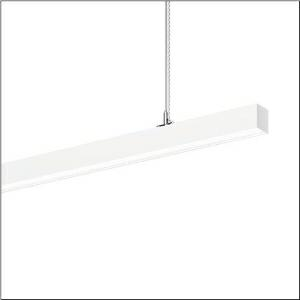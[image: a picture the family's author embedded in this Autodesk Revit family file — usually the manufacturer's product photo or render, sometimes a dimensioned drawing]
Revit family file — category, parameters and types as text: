
# Revit family: silica_r__21_51mx33dc3dwb_1062
name_source: partatom
category: Lighting Fixtures
units: mm (PartAtom-declared; Revit-internal decimal feet)

## family parameters
Cut with Voids When Loaded = No
Host = Face
Light Source = No
Part Type = Normal
Room Calculation Point = No
Round Connector Dimension = Use Diameter
Shared = No

## types (1)
- --- (1 x LED, 14780 lm, 99.5 W, 3000K)
    Apparent Load = 100 VA
    CIE Flux Codes = 78 96 99 55 100
    Color Rendering = 80
    Color Temperature = 3000K
    Default Elevation = 1800 mm
    Description = Silica® 21, office luminaire, primary optical cover: prismatic diffuser, of PMMA, CAT 2 (L<= 3000cd/m²), light emission: direct/indirect distribution, primary light characteristic: symmetric, installation type: suspended mounting, LED, rated luminous flux: 14.780lm, luminous efficacy: 149lm/W, light colour: 830, colour temperature: 3000K, control gear: DALI 2, with terminal, 3+2-pole, max. 2.5mm², mains connection: 220..240V, AC, 50/60Hz, rated input power: 99.5W, luminaire housing, of aluminium, traffic white (RAL 9016), length: 3.004mm, width: 53mm, height: 53mm, protection rating (complete): IP20, insulation class (complete): insulation class I (protective earthing), certification: CE, permissible operating ambient temperature: 0..+35°C, standard: EN 50419, packaging unit: 1 piece
    Height = 53 mm
    Lamp = 1 x LED
    Lamp Light Flux = 14780 lm
    Lamp Power = 99.5 W
    Lamp count = 1
    Length = 3004 mm
    Luminous efficacy = 149 lm/W
    Manufacturer = Siteco
    ModVariant = No
    Model = 51MX33DC3DWB
    Mounting Place = Ceiling
    Mounting Type = Pendant
    Number of Poles = 1
    OnlyDefault = Yes
    Power Factor = 1
    Product Name = Silica® 21
    Product group = office luminaire | ceiling pendant
    ProductGroupID = 903
    Protection Class = Protection class I
    Protection Degree = IP 20
    RLX_Detail_Level = 1
    RLX_Emergency_Light_Flux = 0 lm
    RLX_Emergency_Type = 0
    RLX_Emergency_Type_DB = No
    RlxData = <blob elided: 21489 chars, md5=d20ec6c7>
    Socket = socket
    Standby Power = 0 W
    System Light Flux = 14780 lm
    System Power = 100 W
    Type Comments = factory setting: luminous flux: 100 % | dim-lin: 254 | 345 mA
    Type Image = l_1349007.jpg
    URL = http://relux.com
    VarID = @adj_140315
    Voltage = 0 V
    Weight = 0.00 kg
    Width = 53 mm

## geometry (parser evidence)
native form markers: Blend x4, Sweep x12
no freeform markers — native parametric forms only
